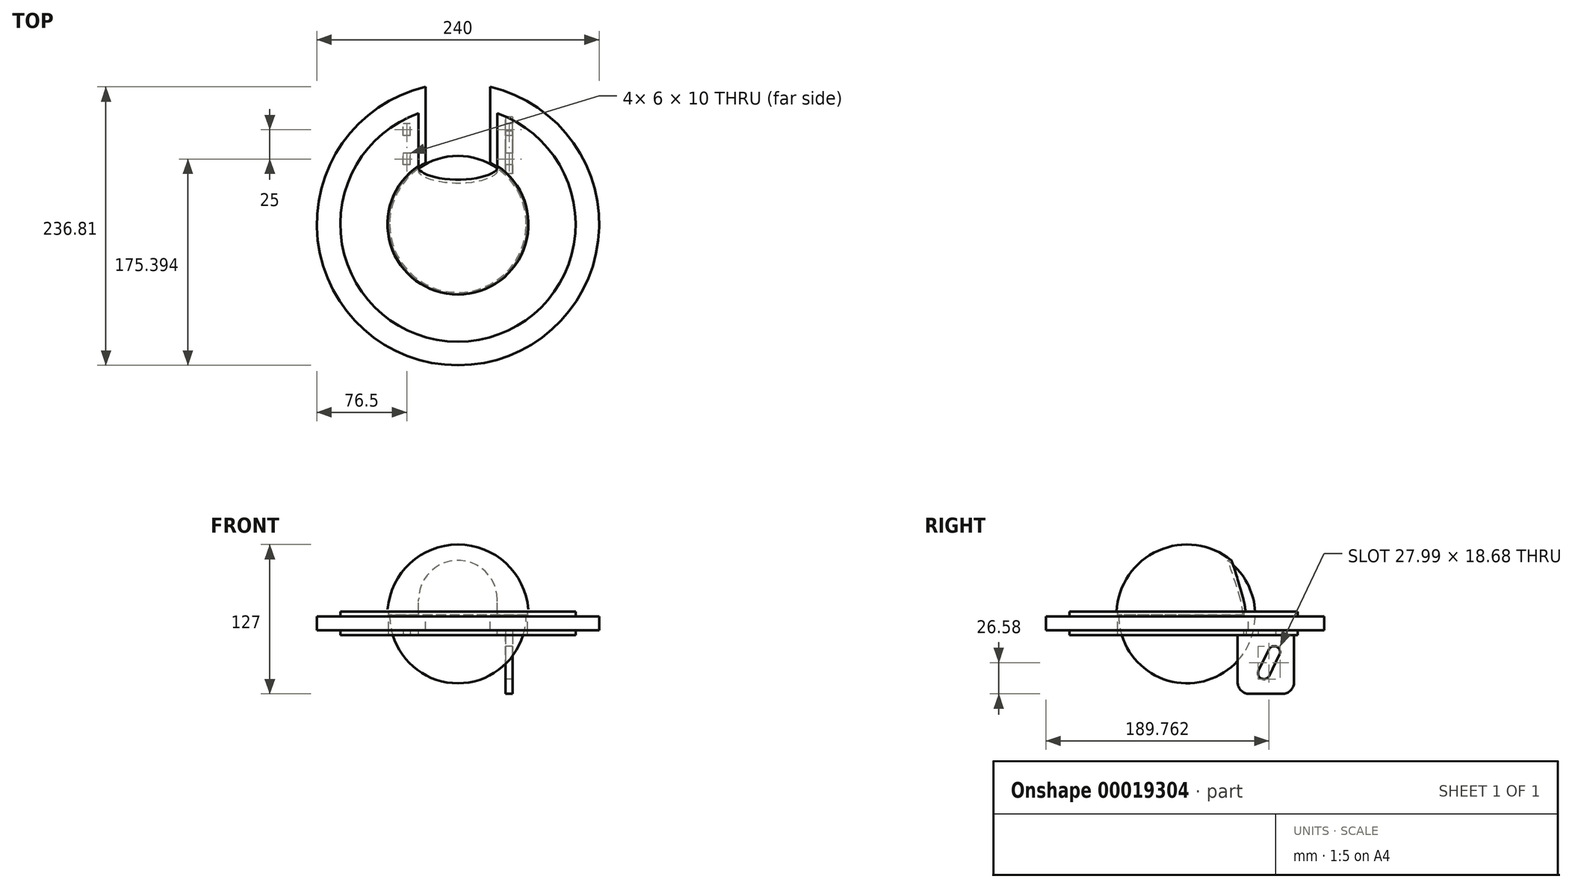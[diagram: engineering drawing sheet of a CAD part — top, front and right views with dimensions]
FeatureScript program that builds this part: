
annotation { "Feature Type Name" : "Feature", "Feature Type Description" : "" }
export const myFeature = defineFeature(function(context is Context, id is Id, definition is map)
    precondition{}
    {
        {
            var Q0;
            Q0=qCreatedBy(makeId("Top.planeOp"),FACE);
            var sketch = newSketch(context, id + "F0", { "sketchPlane" : qUnion([Q0])});
            skArc(sketch, "E0", {"start": v(60, 0) * mm, "mid": v(0, 60) * mm, "end": v(-60, 0) * mm});
            skLineSegment(sketch, "E1", {"start": v(-60, 0) * mm, "end": v(60, 0) * mm});
            skSolve(sketch);
        }
        {
            var Q0;
            Q0=qSketchRegion(id+"F0",true);
            var Q1;
            Q1=sQuery(id+"F0.wireOp",EDGE,"E1");
            revolve(context, id + "F1", {"entities" : qUnion([Q0]), "axis" : qUnion([Q1]), "revolveType" : RevolveType.ONE_DIRECTION, "angle" : 180 * degree});
        }
        {
            var Q0;
            Q0=makeQuery(id+"F1.opRevolve","CAP_FACE",FACE,{"disambiguationData":[OSD([sQuery(id+"F0.wireOp",EDGE,"E0"),sQuery(id+"F0.wireOp",EDGE,"E1")])],"isStart":true});
            shell(context, id + "F2", {"entities" : qUnion([Q0]), "thickness" : 2 * mm});
        }
        {
            var Q0;
            Q0=makeQuery(id+"F1.opRevolve","CAP_FACE",FACE,{"disambiguationData":[OSD([sQuery(id+"F0.wireOp",EDGE,"E0"),sQuery(id+"F0.wireOp",EDGE,"E1")])],"isStart":true});
            var sketch = newSketch(context, id + "F3", { "sketchPlane" : qUnion([Q0])});
            skCircle(sketch, "E2", {"center": v(0, 0) * mm, "radius": 59 * mm});
            skCircle(sketch, "E3.0", {"center": v(0, 0) * mm, "radius": 60 * mm});
            skSolve(sketch);
        }
        {
            var Q0;
            Q0=qSketchRegion(id+"F3",true);
            extrude(context, id + "F4", {"entities" : qUnion([Q0]), "operationType" : NewBodyOperationType.REMOVE, "oppositeDirection" : true, "depth" : 3 * mm});
        }
        {
            var Q0;
            Q0=makeQuery(id+"F4.boolean.opBoolean","COPY",FACE,{"derivedFrom":makeQuery(id+"F4.opExtrude","CAP_FACE",FACE,{"disambiguationData":[OSD([sQuery(id+"F3.wireOp",EDGE,"E2"),sQuery(id+"F3.wireOp",EDGE,"E3.0")])],"isStart":false})});
            var sketch = newSketch(context, id + "F5", { "sketchPlane" : qUnion([Q0])});
            skCircle(sketch, "E4", {"center": v(0, 0) * mm, "radius": 100 * mm});
            skCircle(sketch, "E5.0", {"center": v(0, 0) * mm, "radius": 59 * mm});
            skSolve(sketch);
        }
        {
            var Q0;
            Q0=qSketchRegion(id+"F5",true);
            extrude(context, id + "F6", {"entities" : qUnion([Q0]), "depth" : 4 * mm});
        }
        {
            var Q0;
            Q0=makeQuery(id+"F6.opExtrude","CAP_FACE",FACE,{"disambiguationData":[OSD([sQuery(id+"F5.wireOp",EDGE,"E4"),sQuery(id+"F5.wireOp",EDGE,"E5.0")])],"isStart":false});
            var sketch = newSketch(context, id + "F7", { "sketchPlane" : qUnion([Q0])});
            skCircle(sketch, "E6", {"center": v(0, 0) * mm, "radius": 120 * mm});
            skCircle(sketch, "E7", {"center": v(0, 0) * mm, "radius": 59 * mm});
            skSolve(sketch);
        }
        {
            var Q0;
            Q0=qSketchRegion(id+"F7",true);
            extrude(context, id + "F8", {"entities" : qUnion([Q0]), "depth" : 12 * mm});
        }
        {
            var Q0;
            Q0=makeQuery(id+"F8.opExtrude","CAP_FACE",FACE,{"disambiguationData":[OSD([sQuery(id+"F7.wireOp",EDGE,"E6"),sQuery(id+"F7.wireOp",EDGE,"E7")])],"isStart":false});
            var sketch = newSketch(context, id + "F9", { "sketchPlane" : qUnion([Q0])});
            skCircle(sketch, "E8.0.0", {"center": v(0, 0) * mm, "radius": 100 * mm});
            skCircle(sketch, "E9.0", {"center": v(0, 0) * mm, "radius": 59 * mm});
            skSolve(sketch);
        }
        {
            var Q0;
            Q0=qSketchRegion(id+"F9",true);
            extrude(context, id + "F10", {"entities" : qUnion([Q0]), "depth" : 4 * mm});
        }
        {
            var Q0;
            Q0=qCreatedBy(makeId("Front.planeOp"),FACE);
            var sketch = newSketch(context, id + "F11", { "sketchPlane" : qUnion([Q0])});
            skArc(sketch, "E10", {"start": v(33.5, 13) * mm, "mid": v(0, 46.5) * mm, "end": v(-33.5, 13) * mm});
            skLineSegment(sketch, "E11", {"start": v(-33.5, -32.39) * mm, "end": v(-33.5, -13) * mm});
            skLineSegment(sketch, "E12", {"start": v(33.5, -32.39) * mm, "end": v(33.5, -13) * mm});
            skLineSegment(sketch, "E13", {"start": v(-33.5, -32.39) * mm, "end": v(33.5, -32.39) * mm});
            skLineSegment(sketch, "E14", {"start": v(33.5, -13) * mm, "end": v(27.5, -13) * mm});
            skLineSegment(sketch, "E15", {"start": v(27.5, -13) * mm, "end": v(27.5, -1) * mm});
            skLineSegment(sketch, "E16", {"start": v(27.5, -1) * mm, "end": v(33.5, -1) * mm});
            skLineSegment(sketch, "E17", {"start": v(33.5, -13) * mm, "end": v(33.5, -1) * mm, "construction": true});
            skLineSegment(sketch, "E18", {"start": v(33.5, -1) * mm, "end": v(33.5, 13) * mm});
            skLineSegment(sketch, "E19", {"start": v(0, 0) * mm, "end": v(0, -18.13) * mm, "construction": true});
            skLineSegment(sketch, "E20.0.MirrorCS", {"start": v(-27.5, -13) * mm, "end": v(-27.5, -1) * mm});
            skLineSegment(sketch, "E21.0.MirrorCS", {"start": v(-27.5, -1) * mm, "end": v(-33.5, -1) * mm});
            skLineSegment(sketch, "E22.0.MirrorCS", {"start": v(-33.5, -13) * mm, "end": v(-27.5, -13) * mm});
            skLineSegment(sketch, "E23", {"start": v(-33.5, -1) * mm, "end": v(-33.5, 13) * mm});
            skLineSegment(sketch, "E24", {"start": v(-33.5, -13) * mm, "end": v(-33.5, -1) * mm, "construction": true});
            skSolve(sketch);
        }
        {
            var Q0;
            Q0=qSketchRegion(id+"F11",true);
            extrude(context, id + "F12", {"entities" : qUnion([Q0]), "operationType" : NewBodyOperationType.REMOVE, "endBound" : BoundingType.THROUGH_ALL, "oppositeDirection" : true, "depth" : 25 * mm});
        }
        {
            var Q0;
            Q0=makeQuery(id+"F10.opExtrude","CAP_FACE",FACE,{"disambiguationData":[OSD([sQuery(id+"F9.wireOp",EDGE,"E8.0.0"),sQuery(id+"F9.wireOp",EDGE,"E9.0")])],"isStart":false});
            var sketch = newSketch(context, id + "F13", { "sketchPlane" : qUnion([Q0])});
            skLineSegment(sketch, "E25.bottom", {"start": v(46.5, -50.4) * mm, "end": v(40.5, -50.4) * mm});
            skLineSegment(sketch, "E25.top", {"start": v(46.5, -60.4) * mm, "end": v(40.5, -60.4) * mm});
            skLineSegment(sketch, "E25.left", {"start": v(40.5, -50.4) * mm, "end": v(40.5, -60.4) * mm});
            skLineSegment(sketch, "E25.right", {"start": v(46.5, -50.4) * mm, "end": v(46.5, -60.4) * mm});
            skLineSegment(sketch, "E26.bottom", {"start": v(46.5, -75.4) * mm, "end": v(40.5, -75.4) * mm});
            skLineSegment(sketch, "E26.top", {"start": v(46.5, -85.4) * mm, "end": v(40.5, -85.4) * mm});
            skLineSegment(sketch, "E26.left", {"start": v(40.5, -75.4) * mm, "end": v(40.5, -85.4) * mm});
            skLineSegment(sketch, "E26.right", {"start": v(46.5, -75.4) * mm, "end": v(46.5, -85.4) * mm});
            skLineSegment(sketch, "E27.bottom", {"start": v(-40.5, -50.4) * mm, "end": v(-46.5, -50.4) * mm});
            skLineSegment(sketch, "E27.top", {"start": v(-40.5, -60.4) * mm, "end": v(-46.5, -60.4) * mm});
            skLineSegment(sketch, "E27.left", {"start": v(-40.5, -50.4) * mm, "end": v(-40.5, -60.4) * mm});
            skLineSegment(sketch, "E27.right", {"start": v(-46.5, -50.4) * mm, "end": v(-46.5, -60.4) * mm});
            skLineSegment(sketch, "E28.bottom", {"start": v(-40.5, -75.4) * mm, "end": v(-46.5, -75.4) * mm});
            skLineSegment(sketch, "E28.top", {"start": v(-40.5, -85.4) * mm, "end": v(-46.5, -85.4) * mm});
            skLineSegment(sketch, "E28.left", {"start": v(-40.5, -75.4) * mm, "end": v(-40.5, -85.4) * mm});
            skLineSegment(sketch, "E28.right", {"start": v(-46.5, -75.4) * mm, "end": v(-46.5, -85.4) * mm});
            skLineSegment(sketch, "E29", {"start": v(43.5, -60.4) * mm, "end": v(43.5, -75.4) * mm, "construction": true});
            skLineSegment(sketch, "E30", {"start": v(-43.5, -60.4) * mm, "end": v(-43.5, -75.4) * mm, "construction": true});
            skLineSegment(sketch, "E31", {"start": v(43.5, -71.4) * mm, "end": v(-43.5, -71.4) * mm, "construction": true});
            skPoint(sketch, "E32", {"position": v(0, -71.4) * mm});
            skPoint(sketch, "E33", {"position": v(33.5, -71.4) * mm});
            skSolve(sketch);
        }
        {
            var Q0;
            Q0=qSketchRegion(id+"F13",true);
            extrude(context, id + "F14", {"entities" : qUnion([Q0]), "operationType" : NewBodyOperationType.REMOVE, "oppositeDirection" : true, "depth" : 4 * mm});
        }
        {
            var Q0;
            Q0=makeQuery(id+"F14.boolean.opBoolean","COPY",FACE,{"derivedFrom":makeQuery(id+"F14.opExtrude","SWEPT_FACE",FACE,{"disambiguationData":[OSD([sQuery(id+"F13.wireOp",EDGE,"E25.left")])]})});
            var sketch = newSketch(context, id + "F15", { "sketchPlane" : qUnion([Q0])});
            skLineSegment(sketch, "E34", {"start": v(50.4, -13) * mm, "end": v(50.4, -17) * mm});
            skLineSegment(sketch, "E35", {"start": v(50.4, -17) * mm, "end": v(43.04, -17) * mm});
            skLineSegment(sketch, "E36", {"start": v(43.04, -17) * mm, "end": v(43.04, -67) * mm});
            skLineSegment(sketch, "E37", {"start": v(43.04, -67) * mm, "end": v(91.04, -67) * mm});
            skLineSegment(sketch, "E38", {"start": v(91.04, -67) * mm, "end": v(91.04, -17) * mm});
            skLineSegment(sketch, "E39", {"start": v(91.04, -17) * mm, "end": v(85.4, -17) * mm});
            skLineSegment(sketch, "E40", {"start": v(85.4, -17) * mm, "end": v(85.4, -13) * mm});
            skLineSegment(sketch, "E41", {"start": v(85.4, -13) * mm, "end": v(75.4, -13) * mm});
            skLineSegment(sketch, "E42", {"start": v(75.4, -13) * mm, "end": v(75.4, -17) * mm});
            skLineSegment(sketch, "E43", {"start": v(75.4, -17) * mm, "end": v(60.4, -17) * mm});
            skLineSegment(sketch, "E44", {"start": v(60.4, -17) * mm, "end": v(60.4, -13) * mm});
            skLineSegment(sketch, "E45", {"start": v(60.4, -13) * mm, "end": v(50.4, -13) * mm});
            skLineSegment(sketch, "E46", {"start": v(69.6, -29.24) * mm, "end": v(60.91, -47.25) * mm});
            skLineSegment(sketch, "E47", {"start": v(78.61, -33.59) * mm, "end": v(69.92, -51.6) * mm});
            skArc(sketch, "E48", {"start": v(78.61, -33.59) * mm, "mid": v(76.28, -26.91) * mm, "end": v(69.6, -29.24) * mm});
            skArc(sketch, "E49", {"start": v(60.91, -47.25) * mm, "mid": v(63.24, -53.93) * mm, "end": v(69.92, -51.6) * mm});
            skSolve(sketch);
        }
        {
            var Q0;
            Q0=qSketchRegion(id+"F15",true);
            extrude(context, id + "F16", {"entities" : qUnion([Q0]), "depth" : 6 * mm});
        }
        {
            var Q0;
            Q0=makeQuery(id+"F16.opExtrude","SWEPT_EDGE",EDGE,{"disambiguationData":[OSD([sQuery(id+"F15.wireOp",EDGE,"E36"),sQuery(id+"F15.wireOp",EDGE,"E37")])]});
            var Q1;
            Q1=makeQuery(id+"F16.opExtrude","SWEPT_EDGE",EDGE,{"disambiguationData":[OSD([sQuery(id+"F15.wireOp",EDGE,"E37"),sQuery(id+"F15.wireOp",EDGE,"E38")])]});
            fillet(context, id + "F17", {"entities" : qUnion([Q0, Q1]), "radius" : 10 * mm, "tangentPropagation" : true, "allowEdgeOverflow" : false});
        }
    });
